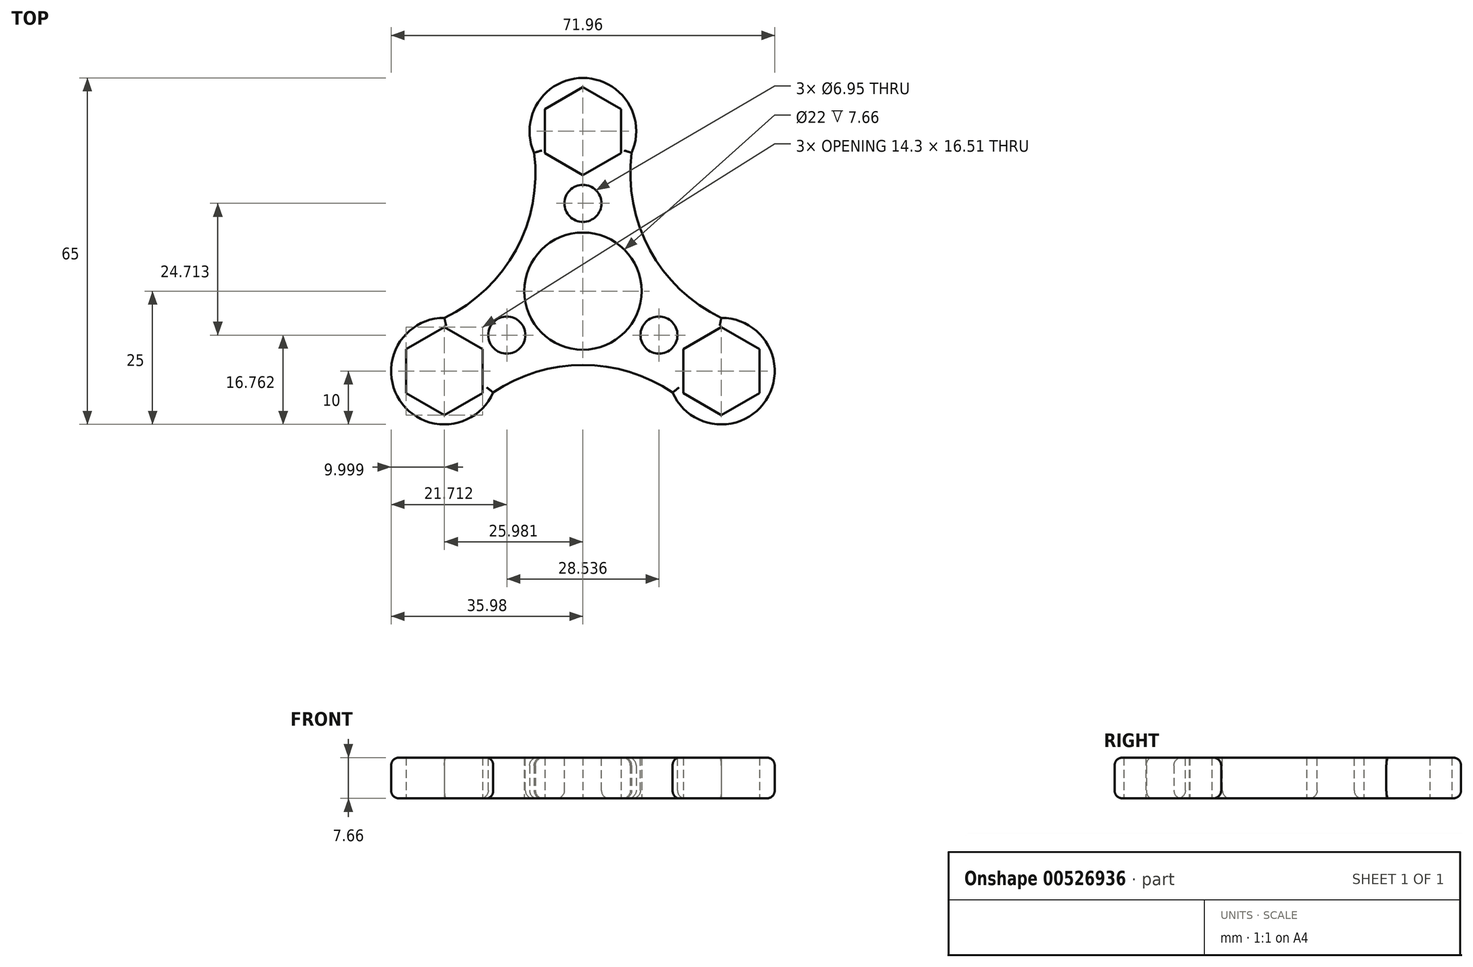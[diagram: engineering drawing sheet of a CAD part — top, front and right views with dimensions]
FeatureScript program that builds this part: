
annotation { "Feature Type Name" : "Feature", "Feature Type Description" : "" }
export const myFeature = defineFeature(function(context is Context, id is Id, definition is map)
    precondition{}
    {
        {
            var Q0;
            Q0=qCreatedBy(makeId("Top.planeOp"),FACE);
            var sketch = newSketch(context, id + "F0", { "sketchPlane" : qUnion([Q0])});
            skCircle(sketch, "E0", {"center": v(0, 0) * mm, "radius": 11 * mm});
            skLineSegment(sketch, "E1", {"start": v(0, 30) * mm, "end": v(0, 0) * mm});
            skLineSegment(sketch, "E2.0", {"start": v(-25.98, 15) * mm, "end": v(25.98, 15) * mm});
            skLineSegment(sketch, "E2.1", {"start": v(25.98, 15) * mm, "end": v(0, -30) * mm});
            skLineSegment(sketch, "E2.2", {"start": v(0, -30) * mm, "end": v(-25.98, 15) * mm});
            skPoint(sketch, "E2.0.midPoint", {"position": v(0, 15) * mm});
            skLineSegment(sketch, "E3", {"start": v(0, 0) * mm, "end": v(25.98, -15) * mm});
            skLineSegment(sketch, "E4", {"start": v(25.98, -15) * mm, "end": v(0, 0) * mm});
            skLineSegment(sketch, "E5", {"start": v(0, 0) * mm, "end": v(-25.98, -15) * mm});
            skLineSegment(sketch, "E6", {"start": v(-25.98, -15) * mm, "end": v(0, 0) * mm});
            skCircle(sketch, "E7", {"center": v(-25.98, -15) * mm, "radius": 10 * mm});
            skCircle(sketch, "E8", {"center": v(25.98, -15) * mm, "radius": 10 * mm});
            skCircle(sketch, "E9", {"center": v(0, 30) * mm, "radius": 10 * mm});
            skArc(sketch, "E10", {"start": v(16.83, -19.02) * mm, "mid": v(0, -13.86) * mm, "end": v(-16.83, -19.03) * mm});
            skArc(sketch, "E11", {"start": v(-25.98, -5) * mm, "mid": v(-12.54, 7.76) * mm, "end": v(-9.15, 25.97) * mm});
            skArc(sketch, "E12", {"start": v(9.15, 25.97) * mm, "mid": v(12.54, 7.76) * mm, "end": v(25.98, -5) * mm});
            skLineSegment(sketch, "E13.0", {"start": v(18.83, -19.13) * mm, "end": v(18.83, -10.87) * mm});
            skLineSegment(sketch, "E13.1", {"start": v(18.83, -10.87) * mm, "end": v(25.98, -6.74) * mm});
            skLineSegment(sketch, "E13.2", {"start": v(25.98, -6.74) * mm, "end": v(33.13, -10.87) * mm});
            skLineSegment(sketch, "E13.3", {"start": v(33.13, -10.87) * mm, "end": v(33.13, -19.13) * mm});
            skLineSegment(sketch, "E13.4", {"start": v(33.13, -19.13) * mm, "end": v(25.98, -23.26) * mm});
            skLineSegment(sketch, "E13.5", {"start": v(25.98, -23.26) * mm, "end": v(18.83, -19.13) * mm});
            skPoint(sketch, "E13.0.midPoint", {"position": v(18.83, -15) * mm});
            skLineSegment(sketch, "E14.0", {"start": v(-18.83, -10.87) * mm, "end": v(-18.83, -19.13) * mm});
            skLineSegment(sketch, "E14.1", {"start": v(-18.83, -19.13) * mm, "end": v(-25.98, -23.26) * mm});
            skLineSegment(sketch, "E14.2", {"start": v(-25.98, -23.26) * mm, "end": v(-33.13, -19.13) * mm});
            skLineSegment(sketch, "E14.3", {"start": v(-33.13, -19.13) * mm, "end": v(-33.13, -10.87) * mm});
            skLineSegment(sketch, "E14.4", {"start": v(-33.13, -10.87) * mm, "end": v(-25.98, -6.74) * mm});
            skLineSegment(sketch, "E14.5", {"start": v(-25.98, -6.74) * mm, "end": v(-18.83, -10.87) * mm});
            skPoint(sketch, "E14.0.midPoint", {"position": v(-18.83, -15) * mm});
            skLineSegment(sketch, "E15.0", {"start": v(7.15, 34.13) * mm, "end": v(7.15, 25.87) * mm});
            skLineSegment(sketch, "E15.1", {"start": v(7.15, 25.87) * mm, "end": v(0, 21.74) * mm});
            skLineSegment(sketch, "E15.2", {"start": v(0, 21.74) * mm, "end": v(-7.15, 25.87) * mm});
            skLineSegment(sketch, "E15.3", {"start": v(-7.15, 25.87) * mm, "end": v(-7.15, 34.13) * mm});
            skLineSegment(sketch, "E15.4", {"start": v(-7.15, 34.13) * mm, "end": v(0, 38.26) * mm});
            skLineSegment(sketch, "E15.5", {"start": v(0, 38.26) * mm, "end": v(7.15, 34.13) * mm});
            skPoint(sketch, "E15.0.midPoint", {"position": v(7.15, 30) * mm});
            skSolve(sketch);
        }
        {
            var Q0;
            Q0=makeQuery(id+"F0.imprint","IMPRINT",FACE,{"disambiguationData":[TD([[makeQuery(id+"F0.imprint","IMPRINT",EDGE,{"derivedFrom":sQuery(id+"F0.wireOp",EDGE,"E15.0")}),1.0]])]});
            var Q1;
            {var subQ0=sQuery(id+"F0.wireOp",EDGE,"E9");var subQ1=sQuery(id+"F0.wireOp",EDGE,"E1");var subQ2=makeQuery(id+"F0.imprint","INTERSECT",VERTEX,{"derivedFrom":[subQ1,subQ0]});Q1=makeQuery(id+"F0.imprint","IMPRINT",FACE,{"disambiguationData":[TD([[makeQuery(id+"F0.imprint","IMPRINT",EDGE,{"disambiguationData":[TD([[subQ2,-1.0]])],"derivedFrom":subQ1}),-1.0]])]});}
            var Q2;
            {var subQ0=sQuery(id+"F0.wireOp",EDGE,"E9");var subQ1=sQuery(id+"F0.wireOp",EDGE,"E1");var subQ2=makeQuery(id+"F0.imprint","INTERSECT",VERTEX,{"derivedFrom":[subQ1,subQ0]});Q2=makeQuery(id+"F0.imprint","IMPRINT",FACE,{"disambiguationData":[TD([[makeQuery(id+"F0.imprint","IMPRINT",EDGE,{"disambiguationData":[TD([[subQ2,-1.0]])],"derivedFrom":subQ1}),1.0]])]});}
            var Q3;
            {var subQ7=sQuery(id+"F0.wireOp",EDGE,"E1");var subQ9=sQuery(id+"F0.wireOp",EDGE,"E0");var subQ11=makeQuery(id+"F0.imprint","INTERSECT",VERTEX,{"derivedFrom":[subQ9,subQ7]});Q3=makeQuery(id+"F0.imprint","IMPRINT",FACE,{"disambiguationData":[TD([[makeQuery(id+"F0.imprint","IMPRINT",EDGE,{"disambiguationData":[TD([[subQ11,1.0]])],"derivedFrom":subQ9}),-1.0]])]});}
            var Q4;
            {var subQ3=sQuery(id+"F0.wireOp",EDGE,"E6");var subQ9=sQuery(id+"F0.wireOp",EDGE,"E0");var subQ11=makeQuery(id+"F0.imprint","INTERSECT",VERTEX,{"derivedFrom":[subQ9,subQ3]});Q4=makeQuery(id+"F0.imprint","IMPRINT",FACE,{"disambiguationData":[TD([[makeQuery(id+"F0.imprint","IMPRINT",EDGE,{"disambiguationData":[TD([[subQ11,1.0]])],"derivedFrom":subQ9}),-1.0]])]});}
            var Q5;
            Q5=makeQuery(id+"F0.imprint","IMPRINT",FACE,{"disambiguationData":[TD([[makeQuery(id+"F0.imprint","IMPRINT",EDGE,{"derivedFrom":sQuery(id+"F0.wireOp",EDGE,"E14.0")}),1.0]])]});
            var Q6;
            {var subQ0=sQuery(id+"F0.wireOp",EDGE,"E11");var subQ1=sQuery(id+"F0.wireOp",EDGE,"E2.2");var subQ2=makeQuery(id+"F0.imprint","INTERSECT",VERTEX,{"derivedFrom":[subQ1,subQ0]});Q6=makeQuery(id+"F0.imprint","IMPRINT",FACE,{"disambiguationData":[TD([[makeQuery(id+"F0.imprint","IMPRINT",EDGE,{"disambiguationData":[TD([[subQ2,1.0]])],"derivedFrom":subQ1}),1.0]])]});}
            var Q7;
            {var subQ0=sQuery(id+"F0.wireOp",EDGE,"E10");var subQ1=sQuery(id+"F0.wireOp",EDGE,"E2.2");var subQ2=makeQuery(id+"F0.imprint","INTERSECT",VERTEX,{"derivedFrom":[subQ1,subQ0]});Q7=makeQuery(id+"F0.imprint","IMPRINT",FACE,{"disambiguationData":[TD([[makeQuery(id+"F0.imprint","IMPRINT",EDGE,{"disambiguationData":[TD([[subQ2,-1.0]])],"derivedFrom":subQ1}),1.0]])]});}
            var Q8;
            {var subQ1=sQuery(id+"F0.wireOp",EDGE,"E0");var subQ8=sQuery(id+"F0.wireOp",EDGE,"E6");var subQ11=makeQuery(id+"F0.imprint","INTERSECT",VERTEX,{"derivedFrom":[subQ1,subQ8]});Q8=makeQuery(id+"F0.imprint","IMPRINT",FACE,{"disambiguationData":[TD([[makeQuery(id+"F0.imprint","IMPRINT",EDGE,{"disambiguationData":[TD([[subQ11,-1.0]])],"derivedFrom":subQ1}),-1.0]])]});}
            var Q9;
            {var subQ0=sQuery(id+"F0.wireOp",EDGE,"E10");var subQ1=sQuery(id+"F0.wireOp",EDGE,"E2.1");var subQ2=makeQuery(id+"F0.imprint","INTERSECT",VERTEX,{"derivedFrom":[subQ1,subQ0]});Q9=makeQuery(id+"F0.imprint","IMPRINT",FACE,{"disambiguationData":[TD([[makeQuery(id+"F0.imprint","IMPRINT",EDGE,{"disambiguationData":[TD([[subQ2,1.0]])],"derivedFrom":subQ1}),1.0]])]});}
            var Q10;
            {var subQ0=sQuery(id+"F0.wireOp",EDGE,"E12");var subQ1=sQuery(id+"F0.wireOp",EDGE,"E2.1");var subQ2=makeQuery(id+"F0.imprint","INTERSECT",VERTEX,{"derivedFrom":[subQ1,subQ0]});Q10=makeQuery(id+"F0.imprint","IMPRINT",FACE,{"disambiguationData":[TD([[makeQuery(id+"F0.imprint","IMPRINT",EDGE,{"disambiguationData":[TD([[subQ2,-1.0]])],"derivedFrom":subQ1}),1.0]])]});}
            var Q11;
            Q11=makeQuery(id+"F0.imprint","IMPRINT",FACE,{"disambiguationData":[TD([[makeQuery(id+"F0.imprint","IMPRINT",EDGE,{"derivedFrom":sQuery(id+"F0.wireOp",EDGE,"E13.0")}),1.0]])]});
            extrude(context, id + "F1", {"entities" : qUnion([Q0, Q1, Q2, Q3, Q4, Q5, Q6, Q7, Q8, Q9, Q10, Q11]), "depth" : 7.66 * mm, "offsetDistance" : 25 * mm});
        }
        {
            var Q0;
            Q0=makeQuery(id+"F1.opExtrude","CAP_FACE",FACE,{"disambiguationData":[OSD([sQuery(id+"F0.wireOp",EDGE,"E0"),sQuery(id+"F0.wireOp",EDGE,"6ecd8433-be9a-4efb-821e-c5c08fbd8d0d.0"),sQuery(id+"F0.wireOp",EDGE,"6ecd8433-be9a-4efb-821e-c5c08fbd8d0d.1"),sQuery(id+"F0.wireOp",EDGE,"6ecd8433-be9a-4efb-821e-c5c08fbd8d0d.2"),sQuery(id+"F0.wireOp",EDGE,"6ecd8433-be9a-4efb-821e-c5c08fbd8d0d.3"),sQuery(id+"F0.wireOp",EDGE,"6ecd8433-be9a-4efb-821e-c5c08fbd8d0d.4"),sQuery(id+"F0.wireOp",EDGE,"6ecd8433-be9a-4efb-821e-c5c08fbd8d0d.5"),sQuery(id+"F0.wireOp",EDGE,"1ad9032f-628d-491e-8cbe-ab9449ec9861.0"),sQuery(id+"F0.wireOp",EDGE,"1ad9032f-628d-491e-8cbe-ab9449ec9861.1"),sQuery(id+"F0.wireOp",EDGE,"1ad9032f-628d-491e-8cbe-ab9449ec9861.2"),sQuery(id+"F0.wireOp",EDGE,"1ad9032f-628d-491e-8cbe-ab9449ec9861.3"),sQuery(id+"F0.wireOp",EDGE,"1ad9032f-628d-491e-8cbe-ab9449ec9861.4"),sQuery(id+"F0.wireOp",EDGE,"1ad9032f-628d-491e-8cbe-ab9449ec9861.5"),sQuery(id+"F0.wireOp",EDGE,"2cabaf14-cadd-46fb-af4e-32f49395d764.0"),sQuery(id+"F0.wireOp",EDGE,"2cabaf14-cadd-46fb-af4e-32f49395d764.1"),sQuery(id+"F0.wireOp",EDGE,"2cabaf14-cadd-46fb-af4e-32f49395d764.2"),sQuery(id+"F0.wireOp",EDGE,"2cabaf14-cadd-46fb-af4e-32f49395d764.3"),sQuery(id+"F0.wireOp",EDGE,"2cabaf14-cadd-46fb-af4e-32f49395d764.4"),sQuery(id+"F0.wireOp",EDGE,"2cabaf14-cadd-46fb-af4e-32f49395d764.5"),sQuery(id+"F0.wireOp",EDGE,"E7"),sQuery(id+"F0.wireOp",EDGE,"E8"),sQuery(id+"F0.wireOp",EDGE,"E9"),sQuery(id+"F0.wireOp",EDGE,"E10"),sQuery(id+"F0.wireOp",EDGE,"E11"),sQuery(id+"F0.wireOp",EDGE,"E12")])],"isStart":false});
            var sketch = newSketch(context, id + "F2", { "sketchPlane" : qUnion([Q0])});
            skCircle(sketch, "E16", {"center": v(0, 16.47) * mm, "radius": 3.47 * mm});
            skCircle(sketch, "E17", {"center": v(-14.27, -8.24) * mm, "radius": 3.48 * mm});
            skCircle(sketch, "E18", {"center": v(14.27, -8.24) * mm, "radius": 3.47 * mm});
            skSolve(sketch);
        }
        {
            var Q0;
            Q0=makeQuery(id+"F2.imprint","IMPRINT",FACE,{"disambiguationData":[TD([[makeQuery(id+"F2.imprint","IMPRINT",EDGE,{"derivedFrom":sQuery(id+"F2.wireOp",EDGE,"E16")}),1.0]])]});
            var Q1;
            Q1=makeQuery(id+"F2.imprint","IMPRINT",FACE,{"disambiguationData":[TD([[makeQuery(id+"F2.imprint","IMPRINT",EDGE,{"derivedFrom":sQuery(id+"F2.wireOp",EDGE,"E17")}),1.0]])]});
            var Q2;
            Q2=makeQuery(id+"F2.imprint","IMPRINT",FACE,{"disambiguationData":[TD([[makeQuery(id+"F2.imprint","IMPRINT",EDGE,{"derivedFrom":sQuery(id+"F2.wireOp",EDGE,"E18")}),1.0]])]});
            extrude(context, id + "F3", {"entities" : qUnion([Q0, Q1, Q2]), "operationType" : NewBodyOperationType.REMOVE, "endBound" : BoundingType.THROUGH_ALL, "oppositeDirection" : true, "depth" : 25 * mm, "offsetDistance" : 25 * mm});
        }
        {
            var Q0;
            Q0=makeQuery(id+"F1.opExtrude","CAP_EDGE",EDGE,{"disambiguationData":[OSD([sQuery(id+"F0.wireOp",EDGE,"E11")])],"isStart":false});
            var Q1;
            Q1=makeQuery(id+"F1.opExtrude","CAP_EDGE",EDGE,{"disambiguationData":[OSD([sQuery(id+"F0.wireOp",EDGE,"E9")])],"isStart":false});
            var Q2;
            Q2=makeQuery(id+"F1.opExtrude","CAP_EDGE",EDGE,{"disambiguationData":[OSD([sQuery(id+"F0.wireOp",EDGE,"E12")])],"isStart":false});
            var Q3;
            Q3=makeQuery(id+"F1.opExtrude","CAP_EDGE",EDGE,{"disambiguationData":[OSD([sQuery(id+"F0.wireOp",EDGE,"E10")])],"isStart":false});
            var Q4;
            Q4=makeQuery(id+"F1.opExtrude","CAP_EDGE",EDGE,{"disambiguationData":[OSD([sQuery(id+"F0.wireOp",EDGE,"E7")])],"isStart":false});
            var Q5;
            Q5=makeQuery(id+"F1.opExtrude","CAP_EDGE",EDGE,{"disambiguationData":[OSD([sQuery(id+"F0.wireOp",EDGE,"E8")])],"isStart":false});
            var Q6;
            Q6=makeQuery(id+"F3.boolean.opBoolean","COPY",EDGE,{"derivedFrom":makeQuery(id+"F3.opExtrude","CAP_EDGE",EDGE,{"disambiguationData":[OSD([sQuery(id+"F2.wireOp",EDGE,"E18")])],"isStart":true})});
            var Q7;
            Q7=makeQuery(id+"F3.boolean.opBoolean","COPY",EDGE,{"derivedFrom":makeQuery(id+"F3.opExtrude","CAP_EDGE",EDGE,{"disambiguationData":[OSD([sQuery(id+"F2.wireOp",EDGE,"E17")])],"isStart":true})});
            var Q8;
            Q8=makeQuery(id+"F3.boolean.opBoolean","COPY",EDGE,{"derivedFrom":makeQuery(id+"F3.opExtrude","CAP_EDGE",EDGE,{"disambiguationData":[OSD([sQuery(id+"F2.wireOp",EDGE,"E16")])],"isStart":true})});
            var Q9;
            Q9=makeQuery(id+"F1.opExtrude","CAP_EDGE",EDGE,{"disambiguationData":[OSD([sQuery(id+"F0.wireOp",EDGE,"E10")])],"isStart":true});
            var Q10;
            Q10=makeQuery(id+"F1.opExtrude","CAP_EDGE",EDGE,{"disambiguationData":[OSD([sQuery(id+"F0.wireOp",EDGE,"E11")])],"isStart":true});
            var Q11;
            Q11=makeQuery(id+"F1.opExtrude","CAP_EDGE",EDGE,{"disambiguationData":[OSD([sQuery(id+"F0.wireOp",EDGE,"E9")])],"isStart":true});
            var Q12;
            Q12=makeQuery(id+"F1.opExtrude","CAP_EDGE",EDGE,{"disambiguationData":[OSD([sQuery(id+"F0.wireOp",EDGE,"E12")])],"isStart":true});
            var Q13;
            Q13=makeQuery(id+"F1.opExtrude","CAP_EDGE",EDGE,{"disambiguationData":[OSD([sQuery(id+"F0.wireOp",EDGE,"E8")])],"isStart":true});
            var Q14;
            Q14=makeQuery(id+"F1.opExtrude","CAP_EDGE",EDGE,{"disambiguationData":[OSD([sQuery(id+"F0.wireOp",EDGE,"E7")])],"isStart":true});
            var Q15;
            Q15=makeQuery(id+"F3.boolean.opBoolean","INTERSECT",EDGE,{"derivedFrom":[makeQuery(id+"F1.opExtrude","CAP_FACE",FACE,{"disambiguationData":[OSD([sQuery(id+"F0.wireOp",EDGE,"E0"),sQuery(id+"F0.wireOp",EDGE,"6ecd8433-be9a-4efb-821e-c5c08fbd8d0d.0"),sQuery(id+"F0.wireOp",EDGE,"6ecd8433-be9a-4efb-821e-c5c08fbd8d0d.1"),sQuery(id+"F0.wireOp",EDGE,"6ecd8433-be9a-4efb-821e-c5c08fbd8d0d.2"),sQuery(id+"F0.wireOp",EDGE,"6ecd8433-be9a-4efb-821e-c5c08fbd8d0d.3"),sQuery(id+"F0.wireOp",EDGE,"6ecd8433-be9a-4efb-821e-c5c08fbd8d0d.4"),sQuery(id+"F0.wireOp",EDGE,"6ecd8433-be9a-4efb-821e-c5c08fbd8d0d.5"),sQuery(id+"F0.wireOp",EDGE,"1ad9032f-628d-491e-8cbe-ab9449ec9861.0"),sQuery(id+"F0.wireOp",EDGE,"1ad9032f-628d-491e-8cbe-ab9449ec9861.1"),sQuery(id+"F0.wireOp",EDGE,"1ad9032f-628d-491e-8cbe-ab9449ec9861.2"),sQuery(id+"F0.wireOp",EDGE,"1ad9032f-628d-491e-8cbe-ab9449ec9861.3"),sQuery(id+"F0.wireOp",EDGE,"1ad9032f-628d-491e-8cbe-ab9449ec9861.4"),sQuery(id+"F0.wireOp",EDGE,"1ad9032f-628d-491e-8cbe-ab9449ec9861.5"),sQuery(id+"F0.wireOp",EDGE,"2cabaf14-cadd-46fb-af4e-32f49395d764.0"),sQuery(id+"F0.wireOp",EDGE,"2cabaf14-cadd-46fb-af4e-32f49395d764.1"),sQuery(id+"F0.wireOp",EDGE,"2cabaf14-cadd-46fb-af4e-32f49395d764.2"),sQuery(id+"F0.wireOp",EDGE,"2cabaf14-cadd-46fb-af4e-32f49395d764.3"),sQuery(id+"F0.wireOp",EDGE,"2cabaf14-cadd-46fb-af4e-32f49395d764.4"),sQuery(id+"F0.wireOp",EDGE,"2cabaf14-cadd-46fb-af4e-32f49395d764.5"),sQuery(id+"F0.wireOp",EDGE,"E7"),sQuery(id+"F0.wireOp",EDGE,"E8"),sQuery(id+"F0.wireOp",EDGE,"E9"),sQuery(id+"F0.wireOp",EDGE,"E10"),sQuery(id+"F0.wireOp",EDGE,"E11"),sQuery(id+"F0.wireOp",EDGE,"E12")])],"isStart":true}),makeQuery(id+"F3.opExtrude","SWEPT_FACE",FACE,{"disambiguationData":[OSD([sQuery(id+"F2.wireOp",EDGE,"E17")])]})]});
            var Q16;
            Q16=makeQuery(id+"F3.boolean.opBoolean","INTERSECT",EDGE,{"derivedFrom":[makeQuery(id+"F1.opExtrude","CAP_FACE",FACE,{"disambiguationData":[OSD([sQuery(id+"F0.wireOp",EDGE,"E0"),sQuery(id+"F0.wireOp",EDGE,"6ecd8433-be9a-4efb-821e-c5c08fbd8d0d.0"),sQuery(id+"F0.wireOp",EDGE,"6ecd8433-be9a-4efb-821e-c5c08fbd8d0d.1"),sQuery(id+"F0.wireOp",EDGE,"6ecd8433-be9a-4efb-821e-c5c08fbd8d0d.2"),sQuery(id+"F0.wireOp",EDGE,"6ecd8433-be9a-4efb-821e-c5c08fbd8d0d.3"),sQuery(id+"F0.wireOp",EDGE,"6ecd8433-be9a-4efb-821e-c5c08fbd8d0d.4"),sQuery(id+"F0.wireOp",EDGE,"6ecd8433-be9a-4efb-821e-c5c08fbd8d0d.5"),sQuery(id+"F0.wireOp",EDGE,"1ad9032f-628d-491e-8cbe-ab9449ec9861.0"),sQuery(id+"F0.wireOp",EDGE,"1ad9032f-628d-491e-8cbe-ab9449ec9861.1"),sQuery(id+"F0.wireOp",EDGE,"1ad9032f-628d-491e-8cbe-ab9449ec9861.2"),sQuery(id+"F0.wireOp",EDGE,"1ad9032f-628d-491e-8cbe-ab9449ec9861.3"),sQuery(id+"F0.wireOp",EDGE,"1ad9032f-628d-491e-8cbe-ab9449ec9861.4"),sQuery(id+"F0.wireOp",EDGE,"1ad9032f-628d-491e-8cbe-ab9449ec9861.5"),sQuery(id+"F0.wireOp",EDGE,"2cabaf14-cadd-46fb-af4e-32f49395d764.0"),sQuery(id+"F0.wireOp",EDGE,"2cabaf14-cadd-46fb-af4e-32f49395d764.1"),sQuery(id+"F0.wireOp",EDGE,"2cabaf14-cadd-46fb-af4e-32f49395d764.2"),sQuery(id+"F0.wireOp",EDGE,"2cabaf14-cadd-46fb-af4e-32f49395d764.3"),sQuery(id+"F0.wireOp",EDGE,"2cabaf14-cadd-46fb-af4e-32f49395d764.4"),sQuery(id+"F0.wireOp",EDGE,"2cabaf14-cadd-46fb-af4e-32f49395d764.5"),sQuery(id+"F0.wireOp",EDGE,"E7"),sQuery(id+"F0.wireOp",EDGE,"E8"),sQuery(id+"F0.wireOp",EDGE,"E9"),sQuery(id+"F0.wireOp",EDGE,"E10"),sQuery(id+"F0.wireOp",EDGE,"E11"),sQuery(id+"F0.wireOp",EDGE,"E12")])],"isStart":true}),makeQuery(id+"F3.opExtrude","SWEPT_FACE",FACE,{"disambiguationData":[OSD([sQuery(id+"F2.wireOp",EDGE,"E16")])]})]});
            var Q17;
            Q17=makeQuery(id+"F3.boolean.opBoolean","INTERSECT",EDGE,{"derivedFrom":[makeQuery(id+"F1.opExtrude","CAP_FACE",FACE,{"disambiguationData":[OSD([sQuery(id+"F0.wireOp",EDGE,"E0"),sQuery(id+"F0.wireOp",EDGE,"6ecd8433-be9a-4efb-821e-c5c08fbd8d0d.0"),sQuery(id+"F0.wireOp",EDGE,"6ecd8433-be9a-4efb-821e-c5c08fbd8d0d.1"),sQuery(id+"F0.wireOp",EDGE,"6ecd8433-be9a-4efb-821e-c5c08fbd8d0d.2"),sQuery(id+"F0.wireOp",EDGE,"6ecd8433-be9a-4efb-821e-c5c08fbd8d0d.3"),sQuery(id+"F0.wireOp",EDGE,"6ecd8433-be9a-4efb-821e-c5c08fbd8d0d.4"),sQuery(id+"F0.wireOp",EDGE,"6ecd8433-be9a-4efb-821e-c5c08fbd8d0d.5"),sQuery(id+"F0.wireOp",EDGE,"1ad9032f-628d-491e-8cbe-ab9449ec9861.0"),sQuery(id+"F0.wireOp",EDGE,"1ad9032f-628d-491e-8cbe-ab9449ec9861.1"),sQuery(id+"F0.wireOp",EDGE,"1ad9032f-628d-491e-8cbe-ab9449ec9861.2"),sQuery(id+"F0.wireOp",EDGE,"1ad9032f-628d-491e-8cbe-ab9449ec9861.3"),sQuery(id+"F0.wireOp",EDGE,"1ad9032f-628d-491e-8cbe-ab9449ec9861.4"),sQuery(id+"F0.wireOp",EDGE,"1ad9032f-628d-491e-8cbe-ab9449ec9861.5"),sQuery(id+"F0.wireOp",EDGE,"2cabaf14-cadd-46fb-af4e-32f49395d764.0"),sQuery(id+"F0.wireOp",EDGE,"2cabaf14-cadd-46fb-af4e-32f49395d764.1"),sQuery(id+"F0.wireOp",EDGE,"2cabaf14-cadd-46fb-af4e-32f49395d764.2"),sQuery(id+"F0.wireOp",EDGE,"2cabaf14-cadd-46fb-af4e-32f49395d764.3"),sQuery(id+"F0.wireOp",EDGE,"2cabaf14-cadd-46fb-af4e-32f49395d764.4"),sQuery(id+"F0.wireOp",EDGE,"2cabaf14-cadd-46fb-af4e-32f49395d764.5"),sQuery(id+"F0.wireOp",EDGE,"E7"),sQuery(id+"F0.wireOp",EDGE,"E8"),sQuery(id+"F0.wireOp",EDGE,"E9"),sQuery(id+"F0.wireOp",EDGE,"E10"),sQuery(id+"F0.wireOp",EDGE,"E11"),sQuery(id+"F0.wireOp",EDGE,"E12")])],"isStart":true}),makeQuery(id+"F3.opExtrude","SWEPT_FACE",FACE,{"disambiguationData":[OSD([sQuery(id+"F2.wireOp",EDGE,"E18")])]})]});
            fillet(context, id + "F4", {"entities" : qUnion([Q0, Q1, Q2, Q3, Q4, Q5, Q6, Q7, Q8, Q9, Q10, Q11, Q12, Q13, Q14, Q15, Q16, Q17]), "radius" : 1.5 * mm, "tangentPropagation" : true, "allowEdgeOverflow" : false});
        }
    });
